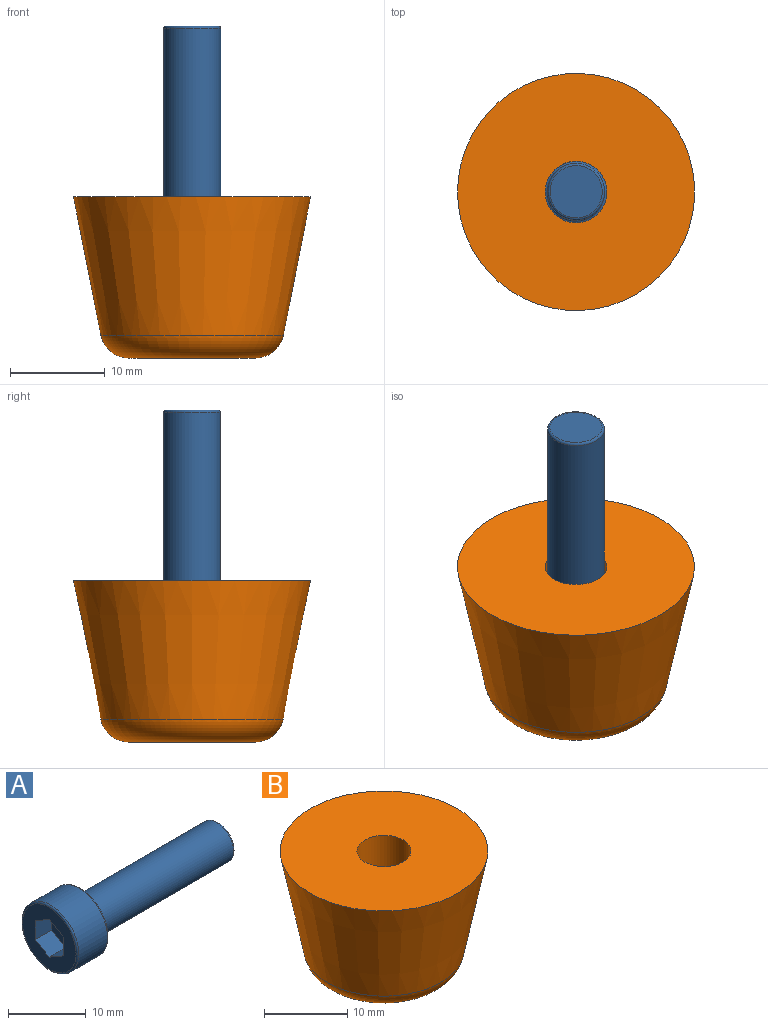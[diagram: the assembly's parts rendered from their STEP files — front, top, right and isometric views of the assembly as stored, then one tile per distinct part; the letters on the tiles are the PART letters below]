
ASSEMBLY  parts=2 mates=1
PART A: 16 faces, bbox 30.7x11.1x11.1 mm
  f0: plane 9.72x9.72mm, normal (-1,0,0), area 51.3mm2, adj f5,f6,f7,f8,f9,f10,f12
  f1: cylinder r=5.11mm len=10.22mm, axis (-1,0,0), area 167mm2, adj f12,f13
  f2: plane 9.72x9.72mm, normal (1,0,0), area 41mm2, adj f13,f14
  f3: cylinder r=3mm len=24.5mm, axis (-1,0,0), area 461.8mm2, adj f14,f15
  f4: plane 5.5x5.5mm, normal (1,0,0), area 23.8mm2, adj f15
  f5: plane 3x2.57mm, normal (0,-0.5,0.87), area 8.9mm2, adj f0,f6,f10,f11
  f6: plane 3x2.57mm, normal (0,0.5,0.87), area 8.9mm2, adj f0,f5,f7,f11
  f7: plane 3x2.97mm, normal (0,1,0), area 8.9mm2, adj f0,f6,f8,f11
  f8: plane 3x2.57mm, normal (0,0.5,-0.87), area 8.9mm2, adj f0,f7,f9,f11
  f9: plane 3x2.57mm, normal (0,-0.5,-0.87), area 8.9mm2, adj f0,f8,f10,f11
  f10: plane 3x2.97mm, normal (0,-1,0), area 8.9mm2, adj f0,f5,f9,f11
  f11: plane 5.94x5.14mm, normal (-1,0,0), area 22.9mm2, adj f5,f6,f7,f8,f9,f10
  f12: torus R=4.86mm, axis (-1,0,0), area 12.4mm2, adj f0,f1
  f13: torus R=4.86mm, axis (-1,0,0), area 12.4mm2, adj f1,f2
  f14: torus R=3.25mm, axis (-1,0,0), area 7.6mm2, adj f2,f3
  f15: torus R=2.75mm, axis (-1,0,0), area 7.2mm2, adj f3,f4
PART B: 8 faces, bbox 25x25x17 mm
  f0: cone r=12.5mm half-angle=11.2deg, axis (0,0,1), area 1032.9mm2, adj f1,f6
  f1: plane 25x25mm, normal (0,0,1), area 457.7mm2, adj f0,f2
  f2: cylinder r=3.25mm len=7mm, axis (0,0,-1), area 142.9mm2, adj f1,f3
  f3: plane 11x11mm, normal (0,0,-1), area 61.9mm2, adj f2,f4
  f4: cylinder r=5.5mm len=11mm, axis (0,0,-1), area 336.9mm2, adj f3,f7
  f5: plane 13.36x13.36mm, normal (0,0,-1), area 36.2mm2, adj f6,f7
  f6: torus R=6.68mm, axis (0,0,1), area 218.8mm2, adj f0,f5
  f7: cone r=5.5mm half-angle=45deg, axis (0,0,-1), area 12.5mm2, adj f4,f5
PLACE A rot(axis=(0,-1,0),90deg) t=(0,0,10)mm
PLACE B at identity fixed
MATE revolute A.f1 <-> B.f0  axis (0,0,1) through (0,0,10)mm
